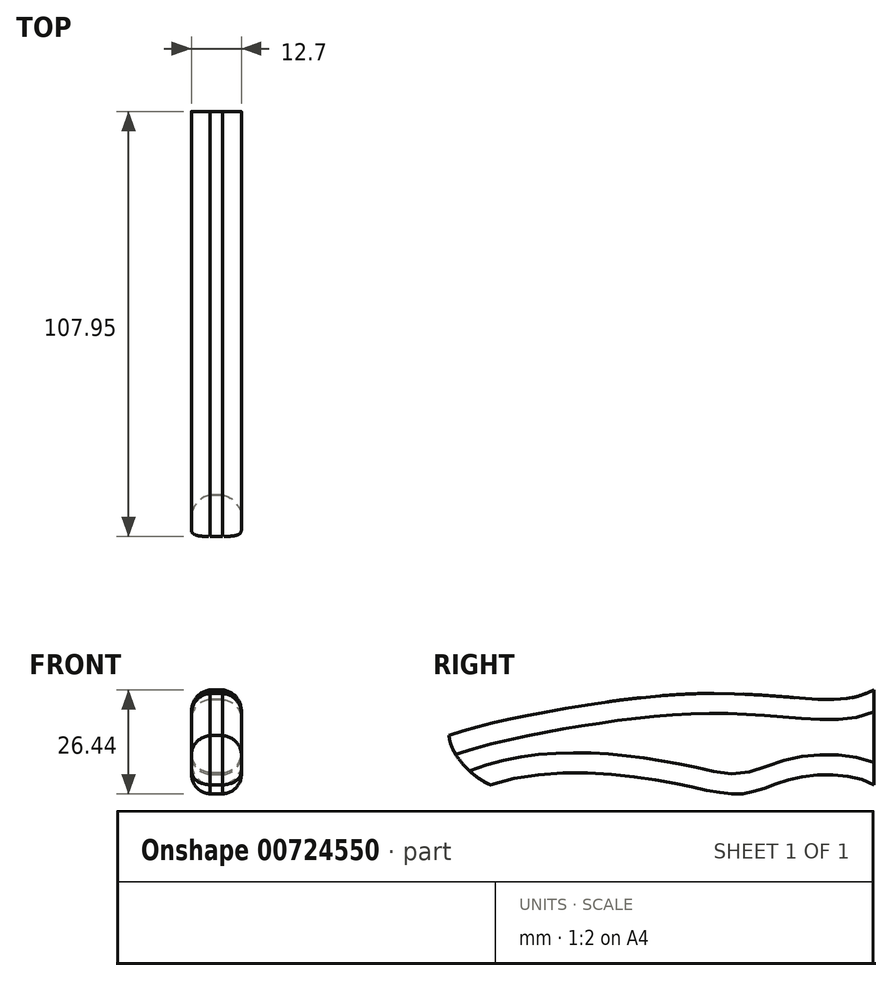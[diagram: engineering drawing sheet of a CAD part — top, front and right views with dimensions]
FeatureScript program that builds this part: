
annotation { "Feature Type Name" : "Feature", "Feature Type Description" : "" }
export const myFeature = defineFeature(function(context is Context, id is Id, definition is map)
    precondition{}
    {
        {
            var Q0;
            Q0=qCreatedBy(makeId("Right.planeOp"),FACE);
            var sketch = newSketch(context, id + "F0", { "sketchPlane" : qUnion([Q0])});
            skLineSegment(sketch, "E0", {"start": v(0, 0) * mm, "end": v(-107.95, 0) * mm, "construction": true});
            skFitSpline(sketch, "E1", {"points": [v(-107.95, 0) * mm, v(-97.47, -12.54) * mm], "startDerivative": vector(0.67, -14.82) * mm, "endDerivative": vector(13.37, -5.48) * mm});
            skFitSpline(sketch, "E2", {"points": [v(-107.95, 0) * mm, v(-86.96, 5.28) * mm, v(-40.4, 10.7) * mm, v(-7.57, 9.28) * mm, v(0, 11.57) * mm], "startDerivative": vector(83.14, 28.46) * mm, "endDerivative": vector(44.55, 19.45) * mm});
            skFitSpline(sketch, "E3", {"points": [v(0, -12.54) * mm, v(-19.28, -10.7) * mm, v(-32.7, -14.7) * mm, v(-49, -12.54) * mm, v(-97.47, -12.54) * mm], "startDerivative": vector(-61.47, 37.4) * mm, "endDerivative": vector(-135.83, -44.52) * mm});
            skLineSegment(sketch, "E4.left", {"start": v(0, -12.54) * mm, "end": v(0, -6.19) * mm});
            skLineSegment(sketch, "E5", {"start": v(0, 0) * mm, "end": v(120.65, 0) * mm, "construction": true});
            skLineSegment(sketch, "E6", {"start": v(0, -6.19) * mm, "end": v(0, 11.57) * mm});
            skSolve(sketch);
        }
        {
            var Q0;
            Q0=qSketchRegion(id+"F0",true);
            extrude(context, id + "F1", {"entities" : qUnion([Q0]), "endBound" : BoundingType.SYMMETRIC, "depth" : 3.17 * mm, "offsetDistance" : 25.4 * mm});
        }
        {
            var Q0;
            Q0=qCreatedBy(makeId("Front.planeOp"),FACE);
            cPlane(context, id + "F2", {"entities" : qUnion([Q0]), "cplaneType" : CPlaneType.OFFSET, "offset" : 4.76 * mm, "oppositeDirection" : true, "width" : 152.4 * mm, "height" : 152.4 * mm});
        }
        {
            var Q0;
            Q0 = qSketchRegion(id + "F0", true);
            extrude(context, id + "F3", {"entities" : qUnion([Q0]), "operationType" : NewBodyOperationType.ADD, "depth" : 6.35 * mm, "offsetDistance" : 25.4 * mm});
        }
        {
            var Q0;
            Q0=makeQuery(id+"F3.opExtrude","CAP_EDGE",EDGE,{"disambiguationData":[OSD([sQuery(id+"F0.wireOp",EDGE,"E2")])],"isStart":false});
            var Q1;
            Q1=makeQuery(id+"F3.opExtrude","CAP_EDGE",EDGE,{"disambiguationData":[OSD([sQuery(id+"F0.wireOp",EDGE,"E3"),sQuery(id+"F0.wireOp",EDGE,"E3")])],"isStart":false});
            fillet(context, id + "F4", {"entities" : qUnion([Q0, Q1]), "radius" : 5.08 * mm, "tangentPropagation" : true, "allowEdgeOverflow" : false});
        }
        {
            var Q0;
            Q0=makeQuery(id+"F1.opExtrude","SWEPT_BODY",BODY,{"disambiguationData":[OSD([sQuery(id+"F0.wireOp",EDGE,"E1"),sQuery(id+"F0.wireOp",EDGE,"E2"),sQuery(id+"F0.wireOp",EDGE,"E3"),sQuery(id+"F0.wireOp",EDGE,"E3"),sQuery(id+"F0.wireOp",EDGE,"E1"),sQuery(id+"F0.wireOp",EDGE,"E4.left"),sQuery(id+"F0.wireOp",EDGE,"E6")])]});
            var Q1;
            Q1=qCreatedBy(makeId("Right.planeOp"),FACE);
            mirror(context, id + "F5", {"entities" : qUnion([Q0]), "mirrorPlane" : qUnion([Q1])});
        }
    });
